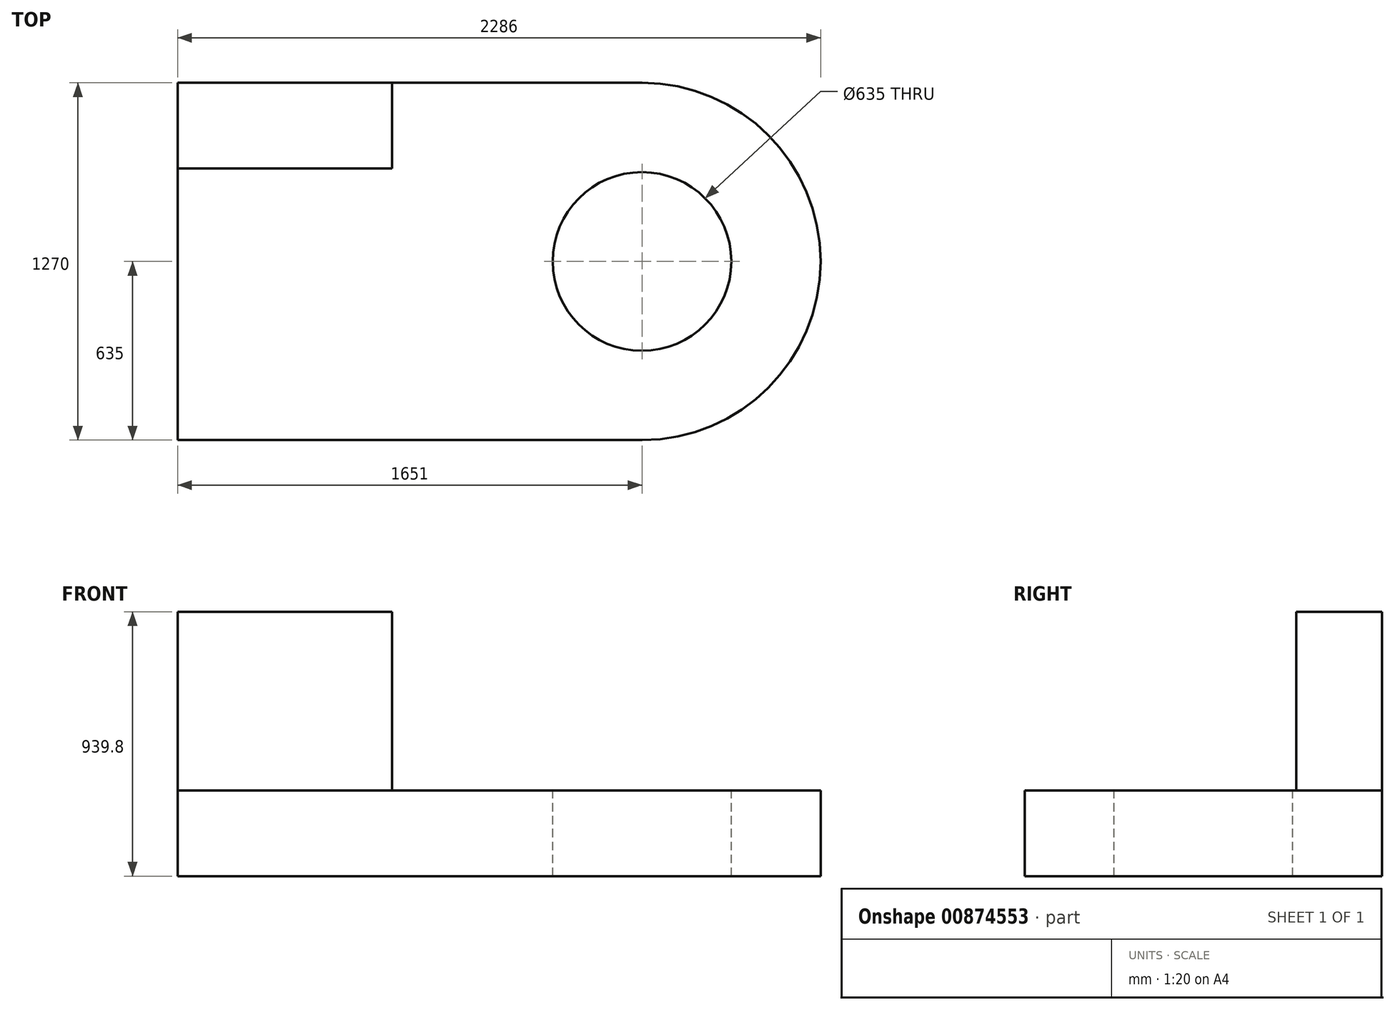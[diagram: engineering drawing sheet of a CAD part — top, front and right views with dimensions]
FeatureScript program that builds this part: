
annotation { "Feature Type Name" : "Feature", "Feature Type Description" : "" }
export const myFeature = defineFeature(function(context is Context, id is Id, definition is map)
    precondition{}
    {
        {
            var Q0;
            Q0=qCreatedBy(makeId("Top.planeOp"),FACE);
            var sketch = newSketch(context, id + "F0", { "sketchPlane" : qUnion([Q0])});
            skLineSegment(sketch, "E0.bottom", {"start": v(0, 0) * mm, "end": v(1651, 0) * mm});
            skLineSegment(sketch, "E0.top", {"start": v(0, -1270) * mm, "end": v(1651, -1270) * mm});
            skLineSegment(sketch, "E0.left", {"start": v(0, 0) * mm, "end": v(0, -1270) * mm});
            skLineSegment(sketch, "E0.right", {"start": v(1651, 0) * mm, "end": v(1651, -1270) * mm});
            skSolve(sketch);
        }
        {
            var Q0;
            Q0=makeQuery(id+"F0.imprint","IMPRINT",FACE,{"disambiguationData":[TD([[makeQuery(id+"F0.imprint","IMPRINT",EDGE,{"derivedFrom":sQuery(id+"F0.wireOp",EDGE,"E0.bottom")}),-1.0]])]});
            extrude(context, id + "F1", {"entities" : qUnion([Q0]), "depth" : 304.8 * mm, "offsetDistance" : 25.4 * mm});
        }
        {
            var Q0;
            Q0=makeQuery(id+"F1.opExtrude","CAP_FACE",FACE,{"disambiguationData":[OSD([sQuery(id+"F0.wireOp",EDGE,"E0.bottom"),sQuery(id+"F0.wireOp",EDGE,"E0.top"),sQuery(id+"F0.wireOp",EDGE,"E0.left"),sQuery(id+"F0.wireOp",EDGE,"E0.right")])],"isStart":false});
            var sketch = newSketch(context, id + "F2", { "sketchPlane" : qUnion([Q0])});
            skLineSegment(sketch, "E1.bottom", {"start": v(0, 0) * mm, "end": v(762, 0) * mm});
            skLineSegment(sketch, "E1.top", {"start": v(0, -304.8) * mm, "end": v(762, -304.8) * mm});
            skLineSegment(sketch, "E1.left", {"start": v(0, 0) * mm, "end": v(0, -304.8) * mm});
            skLineSegment(sketch, "E1.right", {"start": v(762, 0) * mm, "end": v(762, -304.8) * mm});
            skSolve(sketch);
        }
        {
            var Q0;
            Q0=makeQuery(id+"F2.imprint","IMPRINT",FACE,{"disambiguationData":[TD([[makeQuery(id+"F2.imprint","IMPRINT",EDGE,{"derivedFrom":sQuery(id+"F2.wireOp",EDGE,"E1.bottom")}),-1.0]])]});
            extrude(context, id + "F3", {"entities" : qUnion([Q0]), "operationType" : NewBodyOperationType.ADD, "depth" : 635 * mm, "offsetDistance" : 25.4 * mm});
        }
        {
            var Q0;
            Q0=makeQuery(id+"F1.opExtrude","CAP_FACE",FACE,{"disambiguationData":[OSD([sQuery(id+"F0.wireOp",EDGE,"E0.bottom"),sQuery(id+"F0.wireOp",EDGE,"E0.top"),sQuery(id+"F0.wireOp",EDGE,"E0.left"),sQuery(id+"F0.wireOp",EDGE,"E0.right")])],"isStart":false});
            var sketch = newSketch(context, id + "F4", { "sketchPlane" : qUnion([Q0])});
            skCircle(sketch, "E2", {"center": v(1651, -635) * mm, "radius": 635 * mm});
            skSolve(sketch);
        }
        {
            var Q0;
            {var subQ1=makeQuery(id+"F1.opExtrude","CAP_EDGE",EDGE,{"disambiguationData":[OSD([sQuery(id+"F0.wireOp",EDGE,"E0.right")])],"isStart":false});Q0=makeQuery(id+"F4.imprint","IMPRINT",FACE,{"disambiguationData":[TD([[makeQuery(id+"F4.imprint","IMPRINT",EDGE,{"derivedFrom":subQ1}),1.0]])]});}
            extrude(context, id + "F5", {"entities" : qUnion([Q0]), "operationType" : NewBodyOperationType.ADD, "oppositeDirection" : true, "depth" : 304.8 * mm, "offsetDistance" : 25.4 * mm});
        }
        {
            var Q0;
            {var subQ0=sQuery(id+"F0.wireOp",EDGE,"E0.right");Q0=makeQuery(id+"F5.boolean.opBoolean","MERGE",FACE,{"derivedFrom":[makeQuery(id+"F1.opExtrude","CAP_FACE",FACE,{"disambiguationData":[OSD([sQuery(id+"F0.wireOp",EDGE,"E0.bottom"),sQuery(id+"F0.wireOp",EDGE,"E0.top"),sQuery(id+"F0.wireOp",EDGE,"E0.left"),subQ0])],"isStart":false}),makeQuery(id+"F5.opExtrude","CAP_FACE",FACE,{"disambiguationData":[OSD([subQ0,sQuery(id+"F4.wireOp",EDGE,"E2")])],"isStart":true})]});}
            var sketch = newSketch(context, id + "F6", { "sketchPlane" : qUnion([Q0])});
            skCircle(sketch, "E3", {"center": v(1651, -635) * mm, "radius": 317.5 * mm});
            skSolve(sketch);
        }
        {
            var Q0;
            Q0=makeQuery(id+"F6.imprint","IMPRINT",FACE,{"disambiguationData":[TD([[makeQuery(id+"F6.imprint","IMPRINT",EDGE,{"derivedFrom":sQuery(id+"F6.wireOp",EDGE,"E3")}),1.0]])]});
            extrude(context, id + "F7", {"entities" : qUnion([Q0]), "operationType" : NewBodyOperationType.REMOVE, "oppositeDirection" : true, "depth" : 947.42 * mm, "offsetDistance" : 25.4 * mm});
        }
    });
